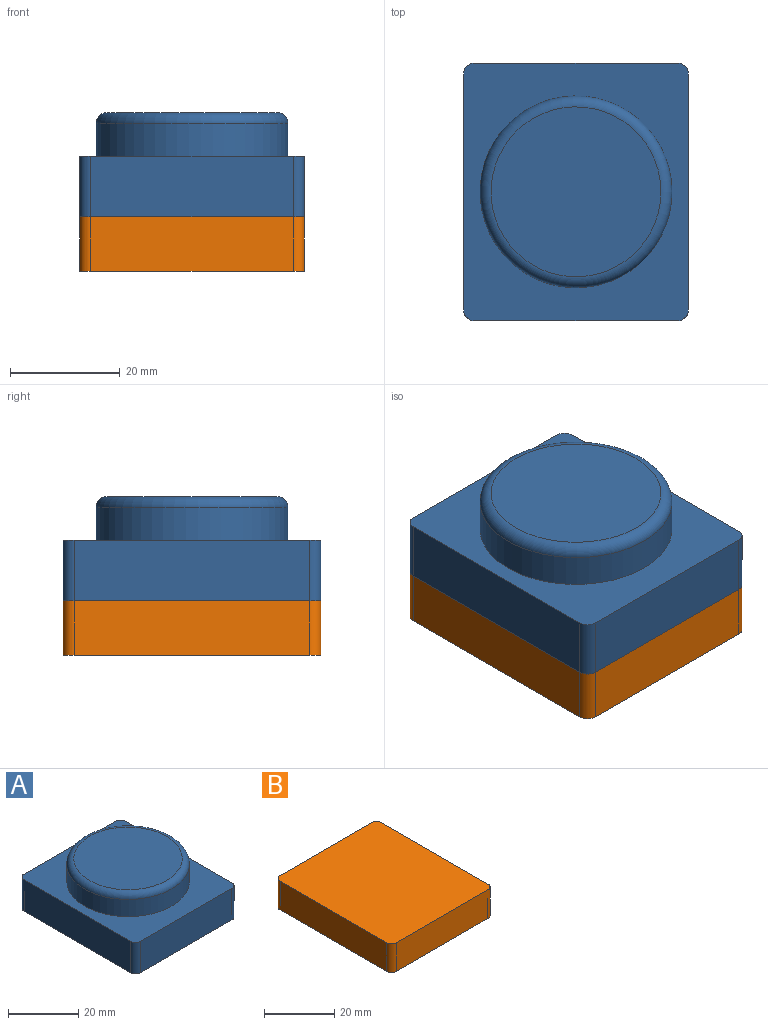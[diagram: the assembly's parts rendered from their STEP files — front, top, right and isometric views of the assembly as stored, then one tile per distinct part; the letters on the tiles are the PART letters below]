
ASSEMBLY  parts=2 mates=1
PART A: 13 faces, bbox 41x47x19 mm
  f0: plane 37x11mm, normal (0,-1,0), area 407mm2, adj f4,f6,f9,f12
  f1: plane 37x11mm, normal (0,1,0), area 407mm2, adj f5,f7,f9,f12
  f2: plane 43x11mm, normal (1,0,0), area 473mm2, adj f6,f7,f9,f12
  f3: plane 43x11mm, normal (-1,0,0), area 473mm2, adj f4,f5,f9,f12
  f4: cylinder r=2mm len=11mm, axis (0,0,-1), area 34.6mm2, adj f0,f3,f9,f12
  f5: cylinder r=2mm len=11mm, axis (0,0,1), area 34.6mm2, adj f1,f3,f9,f12
  f6: cylinder r=2mm len=11mm, axis (0,0,1), area 34.6mm2, adj f0,f2,f9,f12
  f7: cylinder r=2mm len=11mm, axis (0,0,-1), area 34.6mm2, adj f1,f2,f9,f12
  f8: cylinder r=17.5mm len=35mm, axis (0,0,1), area 659.7mm2, adj f9,f11
  f9: plane 47x41mm, normal (0,0,1), area 961.5mm2, adj f0,f1,f2,f3,f4,f5,f6,f7
  f10: plane 31x31mm, normal (0,0,1), area 754.8mm2, adj f11
  f11: torus R=15.5mm, axis (0,0,1), area 331.1mm2, adj f8,f10
  f12: plane 47x41mm, normal (0,0,-1), area 1923.6mm2, adj f0,f1,f2,f3,f4,f5,f6,f7
PART B: 10 faces, bbox 41x47x10 mm
  f0: plane 47x41mm, normal (0,0,-1), area 1923.6mm2, adj f1,f2,f3,f4,f5,f6,f7,f8
  f1: cylinder r=2mm len=10mm, axis (0,0,-1), area 31.4mm2, adj f0,f3,f7,f9
  f2: cylinder r=2mm len=10mm, axis (0,0,1), area 31.4mm2, adj f0,f3,f8,f9
  f3: plane 43x10mm, normal (1,0,0), area 430mm2, adj f0,f1,f2,f9
  f4: cylinder r=2mm len=10mm, axis (0,0,1), area 31.4mm2, adj f0,f6,f7,f9
  f5: cylinder r=2mm len=10mm, axis (0,0,-1), area 31.4mm2, adj f0,f6,f8,f9
  f6: plane 43x10mm, normal (-1,0,0), area 430mm2, adj f0,f4,f5,f9
  f7: plane 37x10mm, normal (0,1,0), area 370mm2, adj f0,f1,f4,f9
  f8: plane 37x10mm, normal (0,-1,0), area 370mm2, adj f0,f2,f5,f9
  f9: plane 47x41mm, normal (0,0,1), area 1923.6mm2, adj f1,f2,f3,f4,f5,f6,f7,f8
PLACE A t=(-30.82,16.71,15.47)mm
PLACE B t=(-30.82,16.71,15.47)mm
MATE fastened A.f8 <-> B.f9  axis (0,0,-1) through (-10.32,-37.06,-41.65)mm
